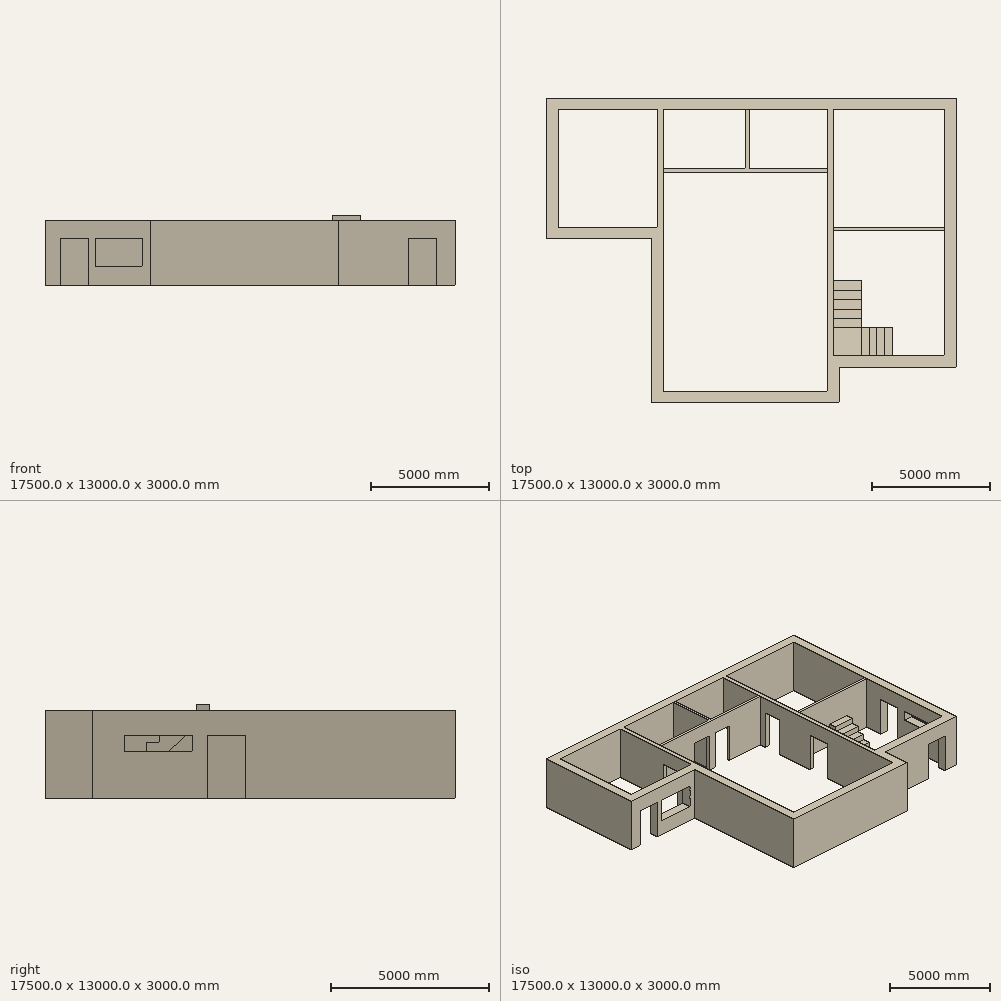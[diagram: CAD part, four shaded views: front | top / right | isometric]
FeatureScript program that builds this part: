
annotation { "Feature Type Name" : "Feature", "Feature Type Description" : "" }
export const myFeature = defineFeature(function(context is Context, id is Id, definition is map)
    precondition{}
    {
        {
            var Q0;
            Q0=qCreatedBy(makeId("Top.planeOp"),FACE);
            var sketch = newSketch(context, id + "F0", { "sketchPlane" : qUnion([Q0])});
            skLineSegment(sketch, "E0", {"start": v(8875, 7625) * mm, "end": v(-8625, 7625) * mm});
            skLineSegment(sketch, "E1", {"start": v(-8625, 7625) * mm, "end": v(-8625, 1625) * mm});
            skLineSegment(sketch, "E2", {"start": v(-8625, 1625) * mm, "end": v(-4125, 1625) * mm});
            skLineSegment(sketch, "E3", {"start": v(-4125, 1625) * mm, "end": v(-4125, -5375) * mm});
            skLineSegment(sketch, "E4", {"start": v(-4125, -5375) * mm, "end": v(3875, -5375) * mm});
            skLineSegment(sketch, "E5", {"start": v(3875, -5375) * mm, "end": v(3875, -3875) * mm});
            skLineSegment(sketch, "E6", {"start": v(3875, -3875) * mm, "end": v(8875, -3875) * mm});
            skLineSegment(sketch, "E7", {"start": v(8875, -3875) * mm, "end": v(8875, 7625) * mm});
            skSolve(sketch);
        }
        {
            var Q0;
            Q0=makeQuery(id+"F0.imprint","IMPRINT",FACE,{"disambiguationData":[TD([[makeQuery(id+"F0.imprint","IMPRINT",EDGE,{"derivedFrom":sQuery(id+"F0.wireOp",EDGE,"E0")}),1.0]])]});
            extrude(context, id + "F1", {"entities" : qUnion([Q0]), "depth" : 2800 * mm, "offsetDistance" : 25 * mm});
        }
        {
            var Q0;
            Q0=qCreatedBy(makeId("Top.planeOp"),FACE);
            var sketch = newSketch(context, id + "F2", { "sketchPlane" : qUnion([Q0])});
            skLineSegment(sketch, "E8", {"start": v(8375, 7125) * mm, "end": v(-3740.25, 7125) * mm});
            skLineSegment(sketch, "E9", {"start": v(-8125, 7125) * mm, "end": v(-8125, 2125) * mm});
            skLineSegment(sketch, "E10", {"start": v(-8125, 2125) * mm, "end": v(-3625, 2125) * mm});
            skLineSegment(sketch, "E11", {"start": v(-3625, 2125) * mm, "end": v(-3625, -4875) * mm});
            skLineSegment(sketch, "E12", {"start": v(-3625, -4875) * mm, "end": v(3375, -4875) * mm});
            skLineSegment(sketch, "E13", {"start": v(3375, -4875) * mm, "end": v(3375, -3375) * mm});
            skLineSegment(sketch, "E14", {"start": v(3375, -3375) * mm, "end": v(8375, -3375) * mm});
            skLineSegment(sketch, "E15", {"start": v(8375, -3375) * mm, "end": v(8375, 7125) * mm});
            skLineSegment(sketch, "E16.trimOffspring", {"start": v(-3740.25, 7125) * mm, "end": v(-8125, 7125) * mm});
            skSolve(sketch);
        }
        {
            var Q0;
            Q0=makeQuery(id+"F2.imprint","IMPRINT",FACE,{"disambiguationData":[TD([[makeQuery(id+"F2.imprint","IMPRINT",EDGE,{"derivedFrom":sQuery(id+"F2.wireOp",EDGE,"E8")}),1.0]])]});
            var Q1;
            Q1=makeQuery(id+"F2.imprint","IMPRINT",FACE,{"disambiguationData":[TD([[makeQuery(id+"F2.imprint","IMPRINT",EDGE,{"derivedFrom":sQuery(id+"F2.wireOp",EDGE,"E9")}),1.0]])]});
            extrude(context, id + "F3", {"entities" : qUnion([Q0, Q1]), "operationType" : NewBodyOperationType.REMOVE, "depth" : 3000 * mm, "offsetDistance" : 25 * mm});
        }
        {
            var Q0;
            Q0=makeQuery(id+"F3.boolean.opBoolean","COPY",FACE,{"derivedFrom":makeQuery(id+"F3.opExtrude","SWEPT_FACE",FACE,{"disambiguationData":[OSD([sQuery(id+"F2.wireOp",EDGE,"E11")])]})});
            var sketch = newSketch(context, id + "F4", { "sketchPlane" : qUnion([Q0])});
            skLineSegment(sketch, "E17.bottom", {"start": v(2125, 0) * mm, "end": v(7125, 0) * mm});
            skLineSegment(sketch, "E17.top", {"start": v(2125, 2800) * mm, "end": v(7125, 2800) * mm});
            skLineSegment(sketch, "E17.left", {"start": v(2125, 0) * mm, "end": v(2125, 2800) * mm});
            skLineSegment(sketch, "E17.right", {"start": v(7125, 0) * mm, "end": v(7125, 2800) * mm});
            skSolve(sketch);
        }
        {
            var Q0;
            Q0=makeQuery(id+"F4.imprint","IMPRINT",FACE,{"disambiguationData":[TD([[makeQuery(id+"F4.imprint","IMPRINT",EDGE,{"derivedFrom":sQuery(id+"F4.wireOp",EDGE,"E17.bottom")}),1.0]])]});
            extrude(context, id + "F5", {"entities" : qUnion([Q0]), "operationType" : NewBodyOperationType.ADD, "oppositeDirection" : true, "depth" : 250 * mm, "offsetDistance" : 25 * mm});
        }
        {
            var Q0;
            Q0 = qSketchRegion(id + "F4", true);
            var sketch = newSketch(context, id + "F6", { "sketchPlane" : qUnion([Q0])});
            skLineSegment(sketch, "E18.bottom", {"start": v(3125, 0) * mm, "end": v(4125, 0) * mm});
            skLineSegment(sketch, "E18.top", {"start": v(3125, 2000) * mm, "end": v(4125, 2000) * mm});
            skLineSegment(sketch, "E18.left", {"start": v(3125, 0) * mm, "end": v(3125, 2000) * mm});
            skLineSegment(sketch, "E18.right", {"start": v(4125, 0) * mm, "end": v(4125, 2000) * mm});
            skSolve(sketch);
        }
        {
            var Q0;
            Q0 = qSketchRegion(id + "F6", true);
            extrude(context, id + "F7", {"entities" : qUnion([Q0]), "operationType" : NewBodyOperationType.REMOVE, "endBound" : BoundingType.UP_TO_NEXT, "oppositeDirection" : true, "depth" : 150 * mm, "offsetDistance" : 25 * mm});
        }
        {
            var Q0;
            Q0=makeQuery(id+"F1.opExtrude","SWEPT_FACE",FACE,{"disambiguationData":[OSD([sQuery(id+"F0.wireOp",EDGE,"E2")])]});
            var sketch = newSketch(context, id + "F8", { "sketchPlane" : qUnion([Q0])});
            skLineSegment(sketch, "E19.bottom", {"start": v(-6775, 0) * mm, "end": v(-7975, 0) * mm});
            skLineSegment(sketch, "E19.top", {"start": v(-6775, 2000) * mm, "end": v(-7975, 2000) * mm});
            skLineSegment(sketch, "E19.left", {"start": v(-6775, 0) * mm, "end": v(-6775, 2000) * mm});
            skLineSegment(sketch, "E19.right", {"start": v(-7975, 0) * mm, "end": v(-7975, 2000) * mm});
            skSolve(sketch);
        }
        {
            var Q0;
            Q0=makeQuery(id+"F8.imprint","IMPRINT",FACE,{"disambiguationData":[TD([[makeQuery(id+"F8.imprint","IMPRINT",EDGE,{"derivedFrom":sQuery(id+"F8.wireOp",EDGE,"E19.bottom")}),1.0]])]});
            extrude(context, id + "F9", {"entities" : qUnion([Q0]), "operationType" : NewBodyOperationType.REMOVE, "endBound" : BoundingType.UP_TO_NEXT, "oppositeDirection" : true, "depth" : 500 * mm, "offsetDistance" : 25 * mm});
        }
        {
            var Q0;
            Q0=makeQuery(id+"F8.imprint","IMPRINT",FACE,{"disambiguationData":[TD([[makeQuery(id+"F8.imprint","IMPRINT",EDGE,{"derivedFrom":sQuery(id+"F8.wireOp",EDGE,"E19.top")}),-1.0]])]});
            var sketch = newSketch(context, id + "F10", { "sketchPlane" : qUnion([Q0])});
            skLineSegment(sketch, "E20.bottom", {"start": v(-6475, 2000) * mm, "end": v(-4475, 2000) * mm});
            skLineSegment(sketch, "E20.top", {"start": v(-6475, 800) * mm, "end": v(-4475, 800) * mm});
            skLineSegment(sketch, "E20.left", {"start": v(-6475, 2000) * mm, "end": v(-6475, 800) * mm});
            skLineSegment(sketch, "E20.right", {"start": v(-4475, 2000) * mm, "end": v(-4475, 800) * mm});
            skSolve(sketch);
        }
        {
            var Q0;
            Q0 = qSketchRegion(id + "F10", true);
            extrude(context, id + "F11", {"entities" : qUnion([Q0]), "operationType" : NewBodyOperationType.REMOVE, "endBound" : BoundingType.UP_TO_NEXT, "oppositeDirection" : true, "depth" : 500 * mm, "offsetDistance" : 25 * mm});
        }
        {
            var Q0;
            Q0=makeQuery(id+"F3.boolean.opBoolean","COPY",FACE,{"derivedFrom":makeQuery(id+"F3.opExtrude","SWEPT_FACE",FACE,{"disambiguationData":[OSD([sQuery(id+"F2.wireOp",EDGE,"E13")])]})});
            var sketch = newSketch(context, id + "F12", { "sketchPlane" : qUnion([Q0])});
            skLineSegment(sketch, "E21.bottom", {"start": v(3375, 0) * mm, "end": v(-7125, 0) * mm});
            skLineSegment(sketch, "E21.top", {"start": v(3375, 2800) * mm, "end": v(-7125, 2800) * mm});
            skLineSegment(sketch, "E21.left", {"start": v(3375, 0) * mm, "end": v(3375, 2800) * mm});
            skLineSegment(sketch, "E21.right", {"start": v(-7125, 0) * mm, "end": v(-7125, 2800) * mm});
            skSolve(sketch);
        }
        {
            var Q0;
            Q0=makeQuery(id+"F12.imprint","IMPRINT",FACE,{"disambiguationData":[TD([[makeQuery(id+"F12.imprint","IMPRINT",EDGE,{"derivedFrom":sQuery(id+"F12.wireOp",EDGE,"E21.bottom")}),-1.0]])]});
            extrude(context, id + "F13", {"entities" : qUnion([Q0]), "operationType" : NewBodyOperationType.ADD, "oppositeDirection" : true, "depth" : 250 * mm, "offsetDistance" : 25 * mm});
        }
        {
            var Q0;
            Q0=makeQuery(id+"F0.imprint","IMPRINT",FACE,{"disambiguationData":[TD([[makeQuery(id+"F0.imprint","IMPRINT",EDGE,{"derivedFrom":sQuery(id+"F0.wireOp",EDGE,"E0")}),1.0]])]});
            var sketch = newSketch(context, id + "F14", { "sketchPlane" : qUnion([Q0])});
            skLineSegment(sketch, "E22.bottom", {"start": v(3375, 4625) * mm, "end": v(25, 4625) * mm});
            skLineSegment(sketch, "E22.top", {"start": v(3375, 4475) * mm, "end": v(-3625, 4475) * mm});
            skLineSegment(sketch, "E22.left", {"start": v(3375, 4625) * mm, "end": v(3375, 4475) * mm});
            skLineSegment(sketch, "E22.right", {"start": v(-3625, 4625) * mm, "end": v(-3625, 4475) * mm});
            skLineSegment(sketch, "E23.top", {"start": v(25, 7125) * mm, "end": v(-125, 7125) * mm});
            skLineSegment(sketch, "E23.left", {"start": v(25, 4625) * mm, "end": v(25, 7125) * mm});
            skLineSegment(sketch, "E23.right", {"start": v(-125, 4625) * mm, "end": v(-125, 7125) * mm});
            skLineSegment(sketch, "E24.trimOffspring", {"start": v(-125, 4625) * mm, "end": v(-3625, 4625) * mm});
            skLineSegment(sketch, "E25.bottom", {"start": v(3625, 2125) * mm, "end": v(8375, 2125) * mm});
            skLineSegment(sketch, "E25.top", {"start": v(3625, 1975) * mm, "end": v(8375, 1975) * mm});
            skLineSegment(sketch, "E25.left", {"start": v(3625, 2125) * mm, "end": v(3625, 1975) * mm});
            skLineSegment(sketch, "E25.right", {"start": v(8375, 2125) * mm, "end": v(8375, 1975) * mm});
            skSolve(sketch);
        }
        {
            var Q0;
            Q0 = qSketchRegion(id + "F14", true);
            extrude(context, id + "F15", {"entities" : qUnion([Q0]), "operationType" : NewBodyOperationType.ADD, "depth" : 2800 * mm, "offsetDistance" : 25 * mm});
        }
        {
            var Q0;
            Q0=makeQuery(id+"F15.opExtrude","SWEPT_FACE",FACE,{"disambiguationData":[OSD([sQuery(id+"F14.wireOp",EDGE,"E24.trimOffspring")])]});
            var sketch = newSketch(context, id + "F16", { "sketchPlane" : qUnion([Q0])});
            skLineSegment(sketch, "E26.bottom", {"start": v(275, 0) * mm, "end": v(1275, 0) * mm});
            skLineSegment(sketch, "E26.top", {"start": v(275, 2000) * mm, "end": v(1275, 2000) * mm});
            skLineSegment(sketch, "E26.left", {"start": v(275, 0) * mm, "end": v(275, 2000) * mm});
            skLineSegment(sketch, "E26.right", {"start": v(1275, 0) * mm, "end": v(1275, 2000) * mm});
            skSolve(sketch);
        }
        {
            var Q0;
            Q0 = qSketchRegion(id + "F16", true);
            extrude(context, id + "F17", {"entities" : qUnion([Q0]), "operationType" : NewBodyOperationType.REMOVE, "endBound" : BoundingType.UP_TO_NEXT, "oppositeDirection" : true, "depth" : 25 * mm, "offsetDistance" : 25 * mm});
        }
        {
            var Q0;
            Q0=makeQuery(id+"F15.opExtrude","SWEPT_FACE",FACE,{"disambiguationData":[OSD([sQuery(id+"F14.wireOp",EDGE,"E22.bottom")])]});
            var sketch = newSketch(context, id + "F18", { "sketchPlane" : qUnion([Q0])});
            skLineSegment(sketch, "E27.bottom", {"start": v(-175, 0) * mm, "end": v(-1175, 0) * mm});
            skLineSegment(sketch, "E27.top", {"start": v(-175, 2000) * mm, "end": v(-1175, 2000) * mm});
            skLineSegment(sketch, "E27.left", {"start": v(-175, 0) * mm, "end": v(-175, 2000) * mm});
            skLineSegment(sketch, "E27.right", {"start": v(-1175, 0) * mm, "end": v(-1175, 2000) * mm});
            skSolve(sketch);
        }
        {
            var Q0;
            Q0 = qSketchRegion(id + "F18", true);
            extrude(context, id + "F19", {"entities" : qUnion([Q0]), "operationType" : NewBodyOperationType.REMOVE, "endBound" : BoundingType.UP_TO_NEXT, "oppositeDirection" : true, "depth" : 25 * mm, "offsetDistance" : 25 * mm});
        }
        {
            var Q0;
            {var subQ0=sQuery(id+"F14.wireOp",EDGE,"E25.bottom");var subQ1=sQuery(id+"F12.wireOp",EDGE,"E21.bottom");var subQ2=sQuery(id+"F12.wireOp",EDGE,"E21.top");Q0=makeQuery(id+"F15.boolean.opBoolean","SPLIT",FACE,{"disambiguationData":[TD([makeQuery(id+"F15.opExtrude","SWEPT_FACE",FACE,{"disambiguationData":[OSD([subQ0])]})])],"derivedFrom":makeQuery(id+"F13.opExtrude","CAP_FACE",FACE,{"disambiguationData":[OSD([subQ1,subQ2,sQuery(id+"F12.wireOp",EDGE,"E21.left"),sQuery(id+"F12.wireOp",EDGE,"E21.right")])],"isStart":false})});}
            var sketch = newSketch(context, id + "F20", { "sketchPlane" : qUnion([Q0])});
            skLineSegment(sketch, "E28.bottom", {"start": v(4125, 0) * mm, "end": v(3125, 0) * mm});
            skLineSegment(sketch, "E28.top", {"start": v(4125, 2000) * mm, "end": v(3125, 2000) * mm});
            skLineSegment(sketch, "E28.left", {"start": v(4125, 0) * mm, "end": v(4125, 2000) * mm});
            skLineSegment(sketch, "E28.right", {"start": v(3125, 0) * mm, "end": v(3125, 2000) * mm});
            skSolve(sketch);
        }
        {
            var Q0;
            Q0 = qSketchRegion(id + "F20", true);
            extrude(context, id + "F21", {"entities" : qUnion([Q0]), "operationType" : NewBodyOperationType.REMOVE, "endBound" : BoundingType.UP_TO_NEXT, "oppositeDirection" : true, "depth" : 25 * mm, "offsetDistance" : 25 * mm});
        }
        {
            var Q0;
            Q0=makeQuery(id+"F1.opExtrude","SWEPT_FACE",FACE,{"disambiguationData":[OSD([sQuery(id+"F0.wireOp",EDGE,"E6")])]});
            var sketch = newSketch(context, id + "F22", { "sketchPlane" : qUnion([Q0])});
            skLineSegment(sketch, "E29.bottom", {"start": v(8075, 0) * mm, "end": v(6875, 0) * mm});
            skLineSegment(sketch, "E29.top", {"start": v(8075, 2000) * mm, "end": v(6875, 2000) * mm});
            skLineSegment(sketch, "E29.left", {"start": v(8075, 0) * mm, "end": v(8075, 2000) * mm});
            skLineSegment(sketch, "E29.right", {"start": v(6875, 0) * mm, "end": v(6875, 2000) * mm});
            skSolve(sketch);
        }
        {
            var Q0;
            Q0 = qSketchRegion(id + "F22", true);
            extrude(context, id + "F23", {"entities" : qUnion([Q0]), "operationType" : NewBodyOperationType.REMOVE, "endBound" : BoundingType.UP_TO_NEXT, "oppositeDirection" : true, "depth" : 25 * mm, "offsetDistance" : 25 * mm});
        }
        {
            var Q0;
            Q0=makeQuery(id+"F1.opExtrude","SWEPT_FACE",FACE,{"disambiguationData":[OSD([sQuery(id+"F0.wireOp",EDGE,"E7")])]});
            var sketch = newSketch(context, id + "F24", { "sketchPlane" : qUnion([Q0])});
            skLineSegment(sketch, "E30.bottom", {"start": v(975, 0) * mm, "end": v(-225, 0) * mm});
            skLineSegment(sketch, "E30.top", {"start": v(975, 2000) * mm, "end": v(-225, 2000) * mm});
            skLineSegment(sketch, "E30.left", {"start": v(975, 0) * mm, "end": v(975, 2000) * mm});
            skLineSegment(sketch, "E30.right", {"start": v(-225, 0) * mm, "end": v(-225, 2000) * mm});
            skSolve(sketch);
        }
        {
            var Q0;
            Q0 = qSketchRegion(id + "F24", true);
            extrude(context, id + "F25", {"entities" : qUnion([Q0]), "operationType" : NewBodyOperationType.REMOVE, "endBound" : BoundingType.UP_TO_NEXT, "oppositeDirection" : true, "depth" : 25 * mm, "offsetDistance" : 25 * mm});
        }
        {
            var Q0;
            Q0=makeQuery(id+"F1.opExtrude","SWEPT_FACE",FACE,{"disambiguationData":[OSD([sQuery(id+"F0.wireOp",EDGE,"E7")])]});
            var sketch = newSketch(context, id + "F26", { "sketchPlane" : qUnion([Q0])});
            skLineSegment(sketch, "E31.bottom", {"start": v(-725, 2000) * mm, "end": v(-2875, 2000) * mm});
            skLineSegment(sketch, "E31.top", {"start": v(-725, 1500) * mm, "end": v(-2875, 1500) * mm});
            skLineSegment(sketch, "E31.left", {"start": v(-725, 2000) * mm, "end": v(-725, 1500) * mm});
            skLineSegment(sketch, "E31.right", {"start": v(-2875, 2000) * mm, "end": v(-2875, 1500) * mm});
            skSolve(sketch);
        }
        {
            var Q0;
            Q0 = qSketchRegion(id + "F26", true);
            extrude(context, id + "F27", {"entities" : qUnion([Q0]), "operationType" : NewBodyOperationType.REMOVE, "endBound" : BoundingType.UP_TO_NEXT, "oppositeDirection" : true, "depth" : 25 * mm, "offsetDistance" : 25 * mm});
        }
        {
            var Q0;
            {var subQ8=sQuery(id+"F12.wireOp",EDGE,"E21.top");var subQ9=sQuery(id+"F12.wireOp",EDGE,"E21.bottom");Q0=makeQuery(id+"F15.boolean.opBoolean","SPLIT",FACE,{"disambiguationData":[TD([makeQuery(id+"F3.boolean.opBoolean","COPY",FACE,{"derivedFrom":makeQuery(id+"F3.opExtrude","SWEPT_FACE",FACE,{"disambiguationData":[OSD([sQuery(id+"F2.wireOp",EDGE,"E12")])]})})])],"derivedFrom":makeQuery(id+"F13.boolean.opBoolean","MERGE",FACE,{"derivedFrom":[makeQuery(id+"F3.boolean.opBoolean","COPY",FACE,{"derivedFrom":makeQuery(id+"F3.opExtrude","SWEPT_FACE",FACE,{"disambiguationData":[OSD([sQuery(id+"F2.wireOp",EDGE,"E13")])]})}),makeQuery(id+"F13.opExtrude","CAP_FACE",FACE,{"disambiguationData":[OSD([subQ9,subQ8,sQuery(id+"F12.wireOp",EDGE,"E21.left"),sQuery(id+"F12.wireOp",EDGE,"E21.right")])],"isStart":true})]})});}
            var sketch = newSketch(context, id + "F28", { "sketchPlane" : qUnion([Q0])});
            skLineSegment(sketch, "E32.bottom", {"start": v(225, 0) * mm, "end": v(-975, 0) * mm});
            skLineSegment(sketch, "E32.top", {"start": v(225, 2000) * mm, "end": v(-975, 2000) * mm});
            skLineSegment(sketch, "E32.left", {"start": v(225, 0) * mm, "end": v(225, 2000) * mm});
            skLineSegment(sketch, "E32.right", {"start": v(-975, 0) * mm, "end": v(-975, 2000) * mm});
            skSolve(sketch);
        }
        {
            var Q0;
            Q0 = qSketchRegion(id + "F28", true);
            extrude(context, id + "F29", {"entities" : qUnion([Q0]), "operationType" : NewBodyOperationType.REMOVE, "endBound" : BoundingType.UP_TO_NEXT, "oppositeDirection" : true, "depth" : 25 * mm, "offsetDistance" : 25 * mm});
        }
        {
            var Q0;
            Q0=makeQuery(id+"F0.imprint","IMPRINT",FACE,{"disambiguationData":[TD([[makeQuery(id+"F0.imprint","IMPRINT",EDGE,{"derivedFrom":sQuery(id+"F0.wireOp",EDGE,"E0")}),1.0]])]});
            var sketch = newSketch(context, id + "F30", { "sketchPlane" : qUnion([Q0])});
            skLineSegment(sketch, "E33.bottom", {"start": v(3625, -3375) * mm, "end": v(6125, -3375) * mm});
            skLineSegment(sketch, "E33.top", {"start": v(3625, -2175) * mm, "end": v(6125, -2175) * mm});
            skLineSegment(sketch, "E33.left", {"start": v(3625, -3375) * mm, "end": v(3625, -2175) * mm});
            skLineSegment(sketch, "E33.right", {"start": v(6125, -3375) * mm, "end": v(6125, -2175) * mm});
            skSolve(sketch);
        }
        {
            var Q0;
            Q0 = qSketchRegion(id + "F30", true);
            extrude(context, id + "F31", {"entities" : qUnion([Q0]), "depth" : 1500 * mm, "offsetDistance" : 25 * mm});
        }
        {
            var Q0;
            Q0=makeQuery(id+"F31.opExtrude","SWEPT_FACE",FACE,{"disambiguationData":[OSD([sQuery(id+"F30.wireOp",EDGE,"E33.bottom")])]});
            var sketch = newSketch(context, id + "F32", { "sketchPlane" : qUnion([Q0])});
            skLineSegment(sketch, "E34", {"start": v(6125, 1500) * mm, "end": v(4825, 1500) * mm});
            skLineSegment(sketch, "E35", {"start": v(4825, 1500) * mm, "end": v(4825, 1200) * mm});
            skLineSegment(sketch, "E36", {"start": v(4825, 1200) * mm, "end": v(5150, 1200) * mm});
            skLineSegment(sketch, "E37", {"start": v(5150, 1200) * mm, "end": v(5150, 900) * mm});
            skLineSegment(sketch, "E38", {"start": v(5150, 900) * mm, "end": v(5475, 900) * mm});
            skLineSegment(sketch, "E39", {"start": v(5475, 900) * mm, "end": v(5475, 600) * mm});
            skLineSegment(sketch, "E40", {"start": v(5475, 600) * mm, "end": v(5800, 600) * mm});
            skLineSegment(sketch, "E41", {"start": v(5800, 600) * mm, "end": v(5800, 300) * mm});
            skLineSegment(sketch, "E42", {"start": v(5800, 300) * mm, "end": v(6125, 300) * mm});
            skLineSegment(sketch, "E43", {"start": v(6125, 300) * mm, "end": v(6125, 1500) * mm});
            skLineSegment(sketch, "E44", {"start": v(3625, 0) * mm, "end": v(3625, 1400) * mm});
            skLineSegment(sketch, "E45", {"start": v(3625, 1400) * mm, "end": v(4400, 1400) * mm});
            skLineSegment(sketch, "E46", {"start": v(4400, 1400) * mm, "end": v(5800, 0) * mm});
            skLineSegment(sketch, "E47", {"start": v(5800, 0) * mm, "end": v(3625, 0) * mm});
            skSolve(sketch);
        }
        {
            var Q0;
            Q0 = qSketchRegion(id + "F32", true);
            extrude(context, id + "F33", {"entities" : qUnion([Q0]), "operationType" : NewBodyOperationType.REMOVE, "endBound" : BoundingType.UP_TO_NEXT, "oppositeDirection" : true, "depth" : 25 * mm, "offsetDistance" : 25 * mm});
        }
        {
            var Q0;
            Q0=makeQuery(id+"F33.boolean.opBoolean","COPY",FACE,{"derivedFrom":makeQuery(id+"F33.opExtrude","SWEPT_FACE",FACE,{"disambiguationData":[OSD([sQuery(id+"F32.wireOp",EDGE,"E45")])]})});
            var sketch = newSketch(context, id + "F34", { "sketchPlane" : qUnion([Q0])});
            skLineSegment(sketch, "E48.bottom", {"start": v(3625, 3375) * mm, "end": v(3725, 3375) * mm});
            skLineSegment(sketch, "E48.top", {"start": v(3625, 3275) * mm, "end": v(3725, 3275) * mm});
            skLineSegment(sketch, "E48.left", {"start": v(3625, 3375) * mm, "end": v(3625, 3275) * mm});
            skLineSegment(sketch, "E48.right", {"start": v(3725, 3375) * mm, "end": v(3725, 3275) * mm});
            skLineSegment(sketch, "E49.bottom", {"start": v(3625, 2175) * mm, "end": v(3725, 2175) * mm});
            skLineSegment(sketch, "E49.top", {"start": v(3625, 2275) * mm, "end": v(3725, 2275) * mm});
            skLineSegment(sketch, "E49.left", {"start": v(3625, 2175) * mm, "end": v(3625, 2275) * mm});
            skLineSegment(sketch, "E49.right", {"start": v(3725, 2175) * mm, "end": v(3725, 2275) * mm});
            skLineSegment(sketch, "E50.bottom", {"start": v(4400, 2175) * mm, "end": v(4300, 2175) * mm});
            skLineSegment(sketch, "E50.top", {"start": v(4400, 2275) * mm, "end": v(4300, 2275) * mm});
            skLineSegment(sketch, "E50.left", {"start": v(4400, 2175) * mm, "end": v(4400, 2275) * mm});
            skLineSegment(sketch, "E50.right", {"start": v(4300, 2175) * mm, "end": v(4300, 2275) * mm});
            skLineSegment(sketch, "E51.bottom", {"start": v(4400, 3375) * mm, "end": v(4300, 3375) * mm});
            skLineSegment(sketch, "E51.top", {"start": v(4400, 3275) * mm, "end": v(4300, 3275) * mm});
            skLineSegment(sketch, "E51.left", {"start": v(4400, 3375) * mm, "end": v(4400, 3275) * mm});
            skLineSegment(sketch, "E51.right", {"start": v(4300, 3375) * mm, "end": v(4300, 3275) * mm});
            skSolve(sketch);
        }
        {
            var Q0;
            Q0 = qSketchRegion(id + "F34", true);
            extrude(context, id + "F35", {"entities" : qUnion([Q0]), "operationType" : NewBodyOperationType.ADD, "depth" : 1400 * mm, "offsetDistance" : 25 * mm});
        }
        {
            var Q0;
            Q0=makeQuery(id+"F33.boolean.opBoolean","COPY",FACE,{"derivedFrom":makeQuery(id+"F33.opExtrude","SWEPT_FACE",FACE,{"disambiguationData":[OSD([sQuery(id+"F32.wireOp",EDGE,"E35")])]})});
            var sketch = newSketch(context, id + "F36", { "sketchPlane" : qUnion([Q0])});
            skLineSegment(sketch, "E52.bottom", {"start": v(-2175, 1200) * mm, "end": v(-175, 1200) * mm});
            skLineSegment(sketch, "E52.top", {"start": v(-2175, 3000) * mm, "end": v(-175, 3000) * mm});
            skLineSegment(sketch, "E52.left", {"start": v(-2175, 1200) * mm, "end": v(-2175, 3000) * mm});
            skLineSegment(sketch, "E52.right", {"start": v(-175, 1200) * mm, "end": v(-175, 3000) * mm});
            skSolve(sketch);
        }
        {
            var Q0;
            {var subQ1=sQuery(id+"F32.wireOp",EDGE,"E35");Q0=makeQuery(id+"F36.imprint","IMPRINT",FACE,{"disambiguationData":[TD([[makeQuery(id+"F36.imprint","IMPRINT",EDGE,{"derivedFrom":makeQuery(id+"F33.boolean.opBoolean","COPY",EDGE,{"derivedFrom":makeQuery(id+"F33.opExtrude","CAP_EDGE",EDGE,{"disambiguationData":[OSD([subQ1])],"isStart":true})})}),1.0]])]});}
            var Q1;
            {var subQ3=sQuery(id+"F36.wireOp",EDGE,"E52.bottom");Q1=makeQuery(id+"F36.imprint","IMPRINT",FACE,{"disambiguationData":[TD([[makeQuery(id+"F36.imprint","IMPRINT",EDGE,{"derivedFrom":subQ3}),1.0]])]});}
            extrude(context, id + "F37", {"entities" : qUnion([Q0, Q1]), "operationType" : NewBodyOperationType.ADD, "oppositeDirection" : true, "depth" : 1200 * mm, "offsetDistance" : 25 * mm});
        }
        {
            var Q0;
            {var subQ0=sQuery(id+"F32.wireOp",EDGE,"E35");Q0=makeQuery(id+"F37.boolean.opBoolean","MERGE",FACE,{"derivedFrom":[makeQuery(id+"F33.boolean.opBoolean","COPY",FACE,{"derivedFrom":makeQuery(id+"F33.opExtrude","SWEPT_FACE",FACE,{"disambiguationData":[OSD([subQ0])]})}),makeQuery(id+"F37.opExtrude","CAP_FACE",FACE,{"disambiguationData":[OSD([sQuery(id+"F30.wireOp",EDGE,"E33.bottom"),sQuery(id+"F32.wireOp",EDGE,"E34"),subQ0,sQuery(id+"F32.wireOp",EDGE,"E36"),sQuery(id+"F36.wireOp",EDGE,"E52.bottom"),sQuery(id+"F36.wireOp",EDGE,"E52.top"),sQuery(id+"F36.wireOp",EDGE,"E52.left"),sQuery(id+"F36.wireOp",EDGE,"E52.right")])],"isStart":true})]});}
            var sketch = newSketch(context, id + "F38", { "sketchPlane" : qUnion([Q0])});
            skLineSegment(sketch, "E53", {"start": v(-2175, 3000) * mm, "end": v(-575, 3000) * mm});
            skLineSegment(sketch, "E54", {"start": v(-575, 3000) * mm, "end": v(-575, 2700) * mm});
            skLineSegment(sketch, "E55", {"start": v(-575, 2700) * mm, "end": v(-975, 2700) * mm});
            skLineSegment(sketch, "E56", {"start": v(-975, 2700) * mm, "end": v(-975, 2400) * mm});
            skLineSegment(sketch, "E57", {"start": v(-975, 2400) * mm, "end": v(-1375, 2400) * mm});
            skLineSegment(sketch, "E58", {"start": v(-1375, 2400) * mm, "end": v(-1375, 2100) * mm});
            skLineSegment(sketch, "E59", {"start": v(-1375, 2100) * mm, "end": v(-1775, 2100) * mm});
            skLineSegment(sketch, "E60", {"start": v(-1775, 2100) * mm, "end": v(-1775, 1800) * mm});
            skLineSegment(sketch, "E61", {"start": v(-1775, 1800) * mm, "end": v(-2175, 1800) * mm});
            skLineSegment(sketch, "E62", {"start": v(-2175, 1800) * mm, "end": v(-2175, 3000) * mm});
            skLineSegment(sketch, "E63", {"start": v(-175, 1200) * mm, "end": v(-175, 2700) * mm});
            skLineSegment(sketch, "E64", {"start": v(-175, 2700) * mm, "end": v(-1775, 1200) * mm});
            skLineSegment(sketch, "E65", {"start": v(-1775, 1200) * mm, "end": v(-175, 1200) * mm});
            skSolve(sketch);
        }
        {
            var Q0;
            Q0 = qSketchRegion(id + "F38", true);
            extrude(context, id + "F39", {"entities" : qUnion([Q0]), "operationType" : NewBodyOperationType.REMOVE, "oppositeDirection" : true, "depth" : 1200 * mm, "offsetDistance" : 25 * mm});
        }
    });
